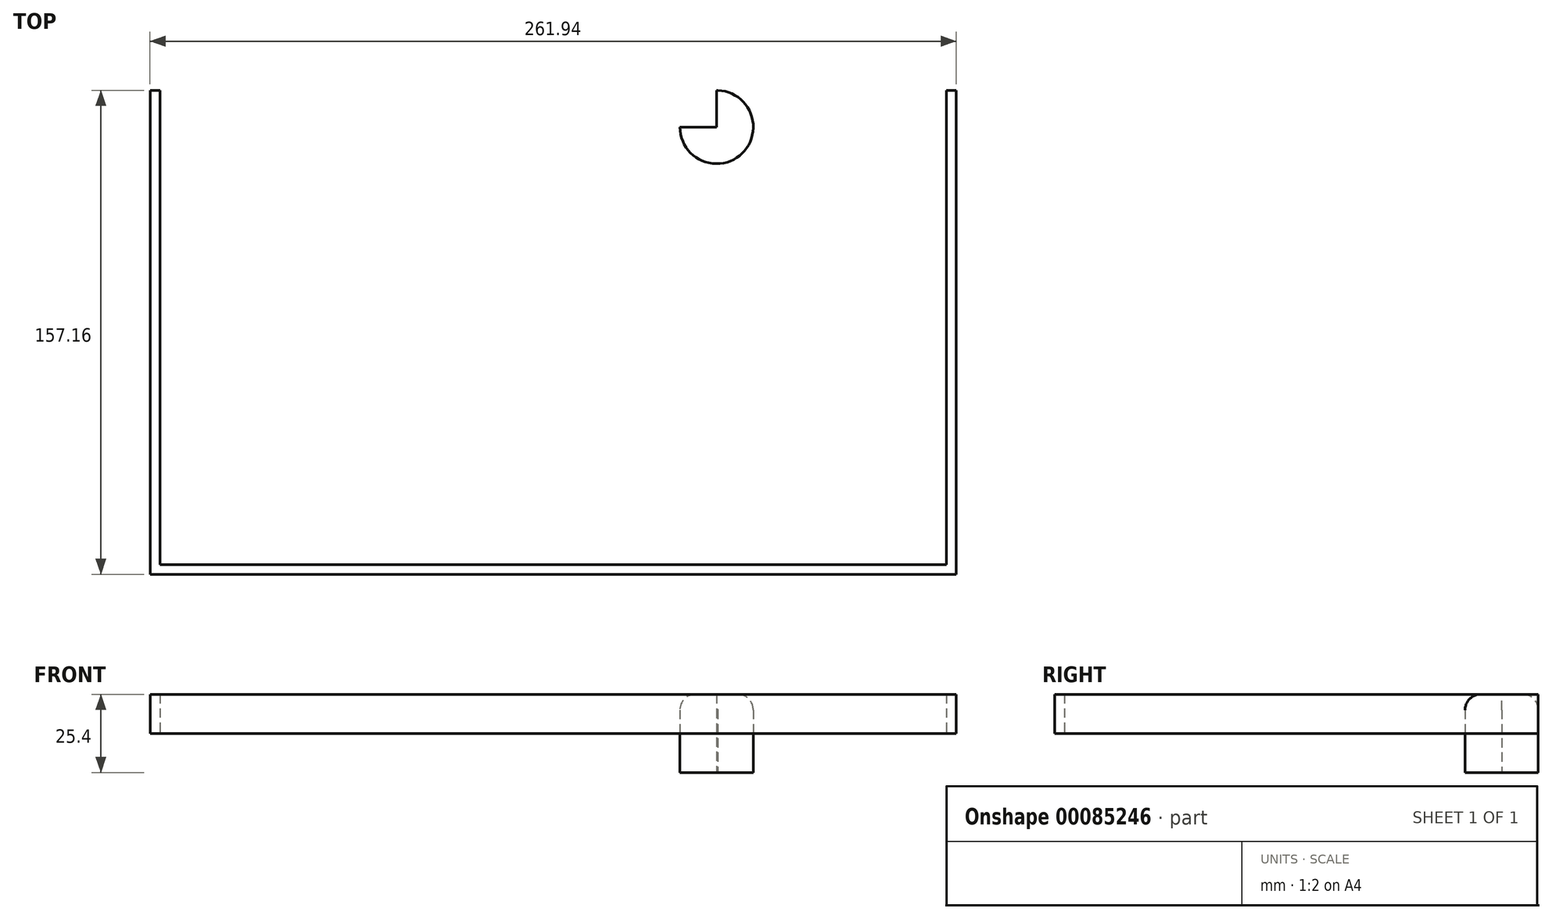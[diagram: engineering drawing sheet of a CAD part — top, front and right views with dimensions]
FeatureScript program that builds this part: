
annotation { "Feature Type Name" : "Feature", "Feature Type Description" : "" }
export const myFeature = defineFeature(function(context is Context, id is Id, definition is map)
    precondition{}
    {
        {
            var Q0;
            Q0=qCreatedBy(makeId("Top.planeOp"),FACE);
            var sketch = newSketch(context, id + "F0", { "sketchPlane" : qUnion([Q0])});
            skLineSegment(sketch, "E0.bottom", {"start": v(-130.97, 78.58) * mm, "end": v(130.97, 78.58) * mm});
            skLineSegment(sketch, "E0.top", {"start": v(-130.97, -78.58) * mm, "end": v(130.97, -78.58) * mm});
            skLineSegment(sketch, "E0.left", {"start": v(-130.97, 78.58) * mm, "end": v(-130.97, -78.58) * mm});
            skLineSegment(sketch, "E0.right", {"start": v(130.97, 78.58) * mm, "end": v(130.97, -78.58) * mm});
            skPoint(sketch, "E0.middle", {"position": v(0, 0) * mm});
            skSolve(sketch);
        }
        {
            var Q0;
            Q0=makeQuery(id+"F0.imprint","IMPRINT",FACE,{"disambiguationData":[TD([[makeQuery(id+"F0.imprint","IMPRINT",EDGE,{"derivedFrom":sQuery(id+"F0.wireOp",EDGE,"E0.bottom")}),-1.0]])]});
            extrude(context, id + "F1", {"entities" : qUnion([Q0]), "depth" : 12.7 * mm});
        }
        {
            var Q0;
            Q0=makeQuery(id+"F1.opExtrude","CAP_FACE",FACE,{"disambiguationData":[OSD([sQuery(id+"F0.wireOp",EDGE,"E0.bottom"),sQuery(id+"F0.wireOp",EDGE,"E0.top"),sQuery(id+"F0.wireOp",EDGE,"E0.left"),sQuery(id+"F0.wireOp",EDGE,"E0.right")])],"isStart":true});
            var sketch = newSketch(context, id + "F2", { "sketchPlane" : qUnion([Q0])});
            skLineSegment(sketch, "E1.bottom", {"start": v(127.8, -78.58) * mm, "end": v(-127.8, -78.58) * mm});
            skLineSegment(sketch, "E1.top", {"start": v(127.8, 75.4) * mm, "end": v(-127.8, 75.4) * mm});
            skLineSegment(sketch, "E1.left", {"start": v(127.8, -78.58) * mm, "end": v(127.8, 75.4) * mm});
            skLineSegment(sketch, "E1.right", {"start": v(-127.8, -78.58) * mm, "end": v(-127.8, 75.4) * mm});
            skSolve(sketch);
        }
        {
            var Q0;
            Q0=makeQuery(id+"F2.imprint","IMPRINT",FACE,{"disambiguationData":[TD([[makeQuery(id+"F2.imprint","IMPRINT",EDGE,{"derivedFrom":sQuery(id+"F2.wireOp",EDGE,"E1.bottom")}),1.0]])]});
            extrude(context, id + "F3", {"entities" : qUnion([Q0]), "operationType" : NewBodyOperationType.ADD, "depth" : 12.7 * mm});
        }
        {
            var Q0;
            Q0=makeQuery(id+"F3.opExtrude","CAP_FACE",FACE,{"disambiguationData":[OSD([sQuery(id+"F2.wireOp",EDGE,"E1.bottom"),sQuery(id+"F2.wireOp",EDGE,"E1.top"),sQuery(id+"F2.wireOp",EDGE,"E1.left"),sQuery(id+"F2.wireOp",EDGE,"E1.right")])],"isStart":false});
            var sketch = newSketch(context, id + "F4", { "sketchPlane" : qUnion([Q0])});
            skPoint(sketch, "E2", {"position": v(0, -68.27) * mm});
            skCircle(sketch, "E3", {"center": v(-10.32, -68.27) * mm, "radius": 10.32 * mm});
            skCircle(sketch, "E4", {"center": v(-30.95, -68.27) * mm, "radius": 10.33 * mm});
            skCircle(sketch, "E5", {"center": v(-53.13, -66.68) * mm, "radius": 11.9 * mm});
            skCircle(sketch, "E6.MirrorC", {"center": v(30.95, -68.27) * mm, "radius": 10.33 * mm});
            skCircle(sketch, "E7.MirrorC", {"center": v(10.32, -68.27) * mm, "radius": 10.32 * mm});
            skCircle(sketch, "E8.MirrorC", {"center": v(53.13, -66.68) * mm, "radius": 11.9 * mm});
            skPoint(sketch, "E9.middle", {"position": v(0, -78.58) * mm});
            skSolve(sketch);
        }
        {
            var Q0;
            {var subQ0=sQuery(id+"F4.wireOp",EDGE,"E4");var subQ1=sQuery(id+"F4.wireOp",EDGE,"E3");var subQ2=makeQuery(id+"F4.imprint","INTERSECT",VERTEX,{"disambiguationData":[OD(0.0)],"derivedFrom":[subQ1,subQ0]});Q0=makeQuery(id+"F4.imprint","IMPRINT",FACE,{"disambiguationData":[TD([[makeQuery(id+"F4.imprint","IMPRINT",EDGE,{"disambiguationData":[TD([[subQ2,1.0]])],"derivedFrom":subQ1}),1.0]])]});}
            var Q1;
            {var subQ0=sQuery(id+"F4.wireOp",EDGE,"E7.MirrorC");var subQ1=sQuery(id+"F4.wireOp",EDGE,"E6.MirrorC");var subQ2=makeQuery(id+"F4.imprint","INTERSECT",VERTEX,{"disambiguationData":[OD(0.0)],"derivedFrom":[subQ1,subQ0]});Q1=makeQuery(id+"F4.imprint","IMPRINT",FACE,{"disambiguationData":[TD([[makeQuery(id+"F4.imprint","IMPRINT",EDGE,{"disambiguationData":[TD([[subQ2,1.0]])],"derivedFrom":subQ1}),-1.0]])]});}
            var Q2;
            {var subQ0=sQuery(id+"F4.wireOp",EDGE,"E3");var subQ1=makeQuery(id+"F3.opExtrude","CAP_EDGE",EDGE,{"disambiguationData":[OSD([sQuery(id+"F2.wireOp",EDGE,"E1.bottom")])],"isStart":false});var subQ2=makeQuery(id+"F4.imprint","INTERSECT",VERTEX,{"disambiguationData":[OD(0.0)],"derivedFrom":[subQ1,subQ0]});Q2=makeQuery(id+"F4.imprint","IMPRINT",FACE,{"disambiguationData":[TD([[makeQuery(id+"F4.imprint","IMPRINT",EDGE,{"disambiguationData":[TD([[subQ2,-1.0]])],"derivedFrom":subQ0}),1.0]])]});}
            var Q3;
            {var subQ0=sQuery(id+"F4.wireOp",EDGE,"E4");var subQ1=makeQuery(id+"F3.opExtrude","CAP_EDGE",EDGE,{"disambiguationData":[OSD([sQuery(id+"F2.wireOp",EDGE,"E1.bottom")])],"isStart":false});var subQ2=makeQuery(id+"F4.imprint","INTERSECT",VERTEX,{"disambiguationData":[OD(0.0)],"derivedFrom":[subQ1,subQ0]});Q3=makeQuery(id+"F4.imprint","IMPRINT",FACE,{"disambiguationData":[TD([[makeQuery(id+"F4.imprint","IMPRINT",EDGE,{"disambiguationData":[TD([[subQ2,-1.0]])],"derivedFrom":subQ0}),1.0]])]});}
            var Q4;
            {var subQ0=sQuery(id+"F4.wireOp",EDGE,"E5");var subQ1=makeQuery(id+"F3.opExtrude","CAP_EDGE",EDGE,{"disambiguationData":[OSD([sQuery(id+"F2.wireOp",EDGE,"E1.bottom")])],"isStart":false});var subQ2=makeQuery(id+"F4.imprint","INTERSECT",VERTEX,{"disambiguationData":[OD(0.0)],"derivedFrom":[subQ1,subQ0]});Q4=makeQuery(id+"F4.imprint","IMPRINT",FACE,{"disambiguationData":[TD([[makeQuery(id+"F4.imprint","IMPRINT",EDGE,{"disambiguationData":[TD([[subQ2,-1.0]])],"derivedFrom":subQ0}),1.0]])]});}
            var Q5;
            {var subQ0=sQuery(id+"F4.wireOp",EDGE,"E6.MirrorC");var subQ1=makeQuery(id+"F3.opExtrude","CAP_EDGE",EDGE,{"disambiguationData":[OSD([sQuery(id+"F2.wireOp",EDGE,"E1.bottom")])],"isStart":false});var subQ2=makeQuery(id+"F4.imprint","INTERSECT",VERTEX,{"disambiguationData":[OD(0.0)],"derivedFrom":[subQ1,subQ0]});Q5=makeQuery(id+"F4.imprint","IMPRINT",FACE,{"disambiguationData":[TD([[makeQuery(id+"F4.imprint","IMPRINT",EDGE,{"disambiguationData":[TD([[subQ2,-1.0]])],"derivedFrom":subQ0}),-1.0]])]});}
            var Q6;
            {var subQ0=sQuery(id+"F4.wireOp",EDGE,"E7.MirrorC");var subQ1=makeQuery(id+"F3.opExtrude","CAP_EDGE",EDGE,{"disambiguationData":[OSD([sQuery(id+"F2.wireOp",EDGE,"E1.bottom")])],"isStart":false});var subQ2=makeQuery(id+"F4.imprint","INTERSECT",VERTEX,{"disambiguationData":[OD(0.0)],"derivedFrom":[subQ1,subQ0]});Q6=makeQuery(id+"F4.imprint","IMPRINT",FACE,{"disambiguationData":[TD([[makeQuery(id+"F4.imprint","IMPRINT",EDGE,{"disambiguationData":[TD([[subQ2,-1.0]])],"derivedFrom":subQ0}),-1.0]])]});}
            var Q7;
            {var subQ0=sQuery(id+"F4.wireOp",EDGE,"E8.MirrorC");var subQ1=makeQuery(id+"F3.opExtrude","CAP_EDGE",EDGE,{"disambiguationData":[OSD([sQuery(id+"F2.wireOp",EDGE,"E1.bottom")])],"isStart":false});var subQ2=makeQuery(id+"F4.imprint","INTERSECT",VERTEX,{"disambiguationData":[OD(0.0)],"derivedFrom":[subQ1,subQ0]});Q7=makeQuery(id+"F4.imprint","IMPRINT",FACE,{"disambiguationData":[TD([[makeQuery(id+"F4.imprint","IMPRINT",EDGE,{"disambiguationData":[TD([[subQ2,-1.0]])],"derivedFrom":subQ0}),-1.0]])]});}
            var Q8;
            {var subQ0=sQuery(id+"F4.wireOp",EDGE,"E8.MirrorC");var subQ1=makeQuery(id+"F3.opExtrude","CAP_EDGE",EDGE,{"disambiguationData":[OSD([sQuery(id+"F2.wireOp",EDGE,"E1.bottom")])],"isStart":false});var subQ2=makeQuery(id+"F4.imprint","INTERSECT",VERTEX,{"disambiguationData":[OD(0.0)],"derivedFrom":[subQ1,subQ0]});Q8=makeQuery(id+"F4.imprint","IMPRINT",FACE,{"disambiguationData":[TD([[makeQuery(id+"F4.imprint","IMPRINT",EDGE,{"disambiguationData":[TD([[subQ2,1.0]])],"derivedFrom":subQ0}),-1.0]])]});}
            var Q9;
            {var subQ0=sQuery(id+"F4.wireOp",EDGE,"E4");var subQ1=sQuery(id+"F4.wireOp",EDGE,"E3");var subQ2=makeQuery(id+"F4.imprint","INTERSECT",VERTEX,{"disambiguationData":[OD(0.0)],"derivedFrom":[subQ1,subQ0]});Q9=makeQuery(id+"F4.imprint","IMPRINT",FACE,{"disambiguationData":[TD([[makeQuery(id+"F4.imprint","IMPRINT",EDGE,{"disambiguationData":[TD([[subQ2,-1.0]])],"derivedFrom":subQ1}),1.0]])]});}
            var Q10;
            {var subQ0=sQuery(id+"F4.wireOp",EDGE,"E7.MirrorC");var subQ1=sQuery(id+"F4.wireOp",EDGE,"E6.MirrorC");var subQ2=makeQuery(id+"F4.imprint","INTERSECT",VERTEX,{"disambiguationData":[OD(0.0)],"derivedFrom":[subQ1,subQ0]});Q10=makeQuery(id+"F4.imprint","IMPRINT",FACE,{"disambiguationData":[TD([[makeQuery(id+"F4.imprint","IMPRINT",EDGE,{"disambiguationData":[TD([[subQ2,-1.0]])],"derivedFrom":subQ1}),-1.0]])]});}
            var Q11;
            {var subQ0=sQuery(id+"F4.wireOp",EDGE,"E7.MirrorC");var subQ1=sQuery(id+"F4.wireOp",EDGE,"E6.MirrorC");var subQ2=makeQuery(id+"F4.imprint","INTERSECT",VERTEX,{"disambiguationData":[OD(0.0)],"derivedFrom":[subQ1,subQ0]});Q11=makeQuery(id+"F4.imprint","IMPRINT",FACE,{"disambiguationData":[TD([[makeQuery(id+"F4.imprint","IMPRINT",EDGE,{"disambiguationData":[TD([[subQ2,1.0]])],"derivedFrom":subQ1}),1.0]])]});}
            var Q12;
            {var subQ0=sQuery(id+"F4.wireOp",EDGE,"E4");var subQ1=sQuery(id+"F4.wireOp",EDGE,"E3");var subQ2=makeQuery(id+"F4.imprint","INTERSECT",VERTEX,{"disambiguationData":[OD(0.0)],"derivedFrom":[subQ1,subQ0]});Q12=makeQuery(id+"F4.imprint","IMPRINT",FACE,{"disambiguationData":[TD([[makeQuery(id+"F4.imprint","IMPRINT",EDGE,{"disambiguationData":[TD([[subQ2,1.0]])],"derivedFrom":subQ1}),-1.0]])]});}
            var Q13;
            {var subQ0=sQuery(id+"F4.wireOp",EDGE,"E5");var subQ1=makeQuery(id+"F3.opExtrude","CAP_EDGE",EDGE,{"disambiguationData":[OSD([sQuery(id+"F2.wireOp",EDGE,"E1.bottom")])],"isStart":false});var subQ2=makeQuery(id+"F4.imprint","INTERSECT",VERTEX,{"disambiguationData":[OD(0.0)],"derivedFrom":[subQ1,subQ0]});Q13=makeQuery(id+"F4.imprint","IMPRINT",FACE,{"disambiguationData":[TD([[makeQuery(id+"F4.imprint","IMPRINT",EDGE,{"disambiguationData":[TD([[subQ2,1.0]])],"derivedFrom":subQ0}),1.0]])]});}
            var Q14;
            {var subQ0=sQuery(id+"F4.wireOp",EDGE,"E4");var subQ1=sQuery(id+"F4.wireOp",EDGE,"E3");var subQ2=makeQuery(id+"F4.imprint","INTERSECT",VERTEX,{"disambiguationData":[OD(0.0)],"derivedFrom":[subQ1,subQ0]});Q14=makeQuery(id+"F4.imprint","IMPRINT",FACE,{"disambiguationData":[TD([[makeQuery(id+"F4.imprint","IMPRINT",EDGE,{"disambiguationData":[TD([[subQ2,-1.0]])],"derivedFrom":subQ1}),-1.0]])]});}
            var Q15;
            {var subQ0=sQuery(id+"F4.wireOp",EDGE,"E7.MirrorC");var subQ1=sQuery(id+"F4.wireOp",EDGE,"E6.MirrorC");var subQ2=makeQuery(id+"F4.imprint","INTERSECT",VERTEX,{"disambiguationData":[OD(1.0)],"derivedFrom":[subQ1,subQ0]});Q15=makeQuery(id+"F4.imprint","IMPRINT",FACE,{"disambiguationData":[TD([[makeQuery(id+"F4.imprint","IMPRINT",EDGE,{"disambiguationData":[TD([[subQ2,1.0]])],"derivedFrom":subQ1}),1.0]])]});}
            extrude(context, id + "F5", {"entities" : qUnion([Q0, Q1, Q2, Q3, Q4, Q5, Q6, Q7, Q8, Q9, Q10, Q11, Q12, Q13, Q14, Q15]), "operationType" : NewBodyOperationType.REMOVE, "endBound" : BoundingType.THROUGH_ALL, "oppositeDirection" : true, "depth" : 25.4 * mm});
        }
        {
            var Q0;
            Q0=makeQuery(id+"F3.opExtrude","CAP_FACE",FACE,{"disambiguationData":[OSD([sQuery(id+"F2.wireOp",EDGE,"E1.bottom"),sQuery(id+"F2.wireOp",EDGE,"E1.top"),sQuery(id+"F2.wireOp",EDGE,"E1.left"),sQuery(id+"F2.wireOp",EDGE,"E1.right")])],"isStart":false});
            var sketch = newSketch(context, id + "F6", { "sketchPlane" : qUnion([Q0])});
            skLineSegment(sketch, "E10.bottom", {"start": v(-53.13, -66.68) * mm, "end": v(53.13, -66.68) * mm});
            skLineSegment(sketch, "E10.top", {"start": v(-53.13, -90.48) * mm, "end": v(53.13, -90.48) * mm});
            skLineSegment(sketch, "E10.left", {"start": v(-53.13, -66.68) * mm, "end": v(-53.13, -90.48) * mm});
            skLineSegment(sketch, "E10.right", {"start": v(53.13, -66.68) * mm, "end": v(53.13, -90.48) * mm});
            skPoint(sketch, "E10.middle", {"position": v(0, -78.58) * mm});
            skSolve(sketch);
        }
        {
            var Q0;
            {var subQ0=sQuery(id+"F6.wireOp",EDGE,"E10.bottom");var subQ1=sQuery(id+"F4.wireOp",EDGE,"E5");var subQ2=makeQuery(id+"F5.boolean.opBoolean","COPY",EDGE,{"derivedFrom":makeQuery(id+"F5.opExtrude","CAP_EDGE",EDGE,{"disambiguationData":[OSD([subQ1])],"isStart":true})});var subQ3=makeQuery(id+"F6.imprint","INTERSECT",VERTEX,{"derivedFrom":[subQ2,subQ0]});Q0=makeQuery(id+"F6.imprint","IMPRINT",FACE,{"disambiguationData":[TD([[makeQuery(id+"F6.imprint","IMPRINT",EDGE,{"disambiguationData":[TD([[subQ3,-1.0]])],"derivedFrom":subQ0}),-1.0]])]});}
            var Q1;
            {var subQ0=sQuery(id+"F6.wireOp",EDGE,"E10.bottom");var subQ1=sQuery(id+"F4.wireOp",EDGE,"E3");var subQ2=makeQuery(id+"F5.boolean.opBoolean","COPY",EDGE,{"derivedFrom":makeQuery(id+"F5.opExtrude","CAP_EDGE",EDGE,{"disambiguationData":[OSD([subQ1])],"isStart":true})});var subQ3=makeQuery(id+"F6.imprint","INTERSECT",VERTEX,{"disambiguationData":[OD(1.0)],"derivedFrom":[subQ2,subQ0]});Q1=makeQuery(id+"F6.imprint","IMPRINT",FACE,{"disambiguationData":[TD([[makeQuery(id+"F6.imprint","IMPRINT",EDGE,{"disambiguationData":[TD([[subQ3,-1.0]])],"derivedFrom":subQ0}),-1.0]])]});}
            var Q2;
            {var subQ0=sQuery(id+"F6.wireOp",EDGE,"E10.bottom");var subQ1=sQuery(id+"F4.wireOp",EDGE,"E8.MirrorC");var subQ2=makeQuery(id+"F5.boolean.opBoolean","COPY",EDGE,{"derivedFrom":makeQuery(id+"F5.opExtrude","CAP_EDGE",EDGE,{"disambiguationData":[OSD([subQ1])],"isStart":true})});var subQ3=makeQuery(id+"F6.imprint","INTERSECT",VERTEX,{"derivedFrom":[subQ2,subQ0]});Q2=makeQuery(id+"F6.imprint","IMPRINT",FACE,{"disambiguationData":[TD([[makeQuery(id+"F6.imprint","IMPRINT",EDGE,{"disambiguationData":[TD([[subQ3,1.0]])],"derivedFrom":subQ0}),-1.0]])]});}
            extrude(context, id + "F7", {"entities" : qUnion([Q0, Q1, Q2]), "operationType" : NewBodyOperationType.REMOVE, "endBound" : BoundingType.THROUGH_ALL, "oppositeDirection" : true, "depth" : 25.4 * mm});
        }
        {
            var Q0;
            Q0=makeQuery(id+"F5.boolean.opBoolean","INTERSECT",EDGE,{"disambiguationData":[OD(0.0)],"derivedFrom":[makeQuery(id+"F3.boolean.opBoolean","MERGE",FACE,{"derivedFrom":[makeQuery(id+"F1.opExtrude","SWEPT_FACE",FACE,{"disambiguationData":[OSD([sQuery(id+"F0.wireOp",EDGE,"E0.bottom")])]}),makeQuery(id+"F3.opExtrude","SWEPT_FACE",FACE,{"disambiguationData":[OSD([sQuery(id+"F2.wireOp",EDGE,"E1.bottom")])]})]}),makeQuery(id+"F5.opExtrude","SWEPT_FACE",FACE,{"disambiguationData":[OSD([sQuery(id+"F4.wireOp",EDGE,"E5")])]})]});
            var Q1;
            Q1=makeQuery(id+"F5.boolean.opBoolean","INTERSECT",EDGE,{"disambiguationData":[OD(0.0)],"derivedFrom":[makeQuery(id+"F3.boolean.opBoolean","MERGE",FACE,{"derivedFrom":[makeQuery(id+"F1.opExtrude","SWEPT_FACE",FACE,{"disambiguationData":[OSD([sQuery(id+"F0.wireOp",EDGE,"E0.bottom")])]}),makeQuery(id+"F3.opExtrude","SWEPT_FACE",FACE,{"disambiguationData":[OSD([sQuery(id+"F2.wireOp",EDGE,"E1.bottom")])]})]}),makeQuery(id+"F5.opExtrude","SWEPT_FACE",FACE,{"disambiguationData":[OSD([sQuery(id+"F4.wireOp",EDGE,"E8.MirrorC")])]})]});
            var Q2;
            Q2=makeQuery(id+"F1.opExtrude","CAP_EDGE",EDGE,{"disambiguationData":[OSD([sQuery(id+"F0.wireOp",EDGE,"E0.top")])],"isStart":false});
            var Q3;
            Q3=makeQuery(id+"F1.opExtrude","CAP_EDGE",EDGE,{"disambiguationData":[OSD([sQuery(id+"F0.wireOp",EDGE,"E0.right")])],"isStart":false});
            var Q4;
            Q4=makeQuery(id+"F1.opExtrude","SWEPT_EDGE",EDGE,{"disambiguationData":[OSD([sQuery(id+"F0.wireOp",EDGE,"E0.top"),sQuery(id+"F0.wireOp",EDGE,"E0.right")])]});
            var Q5;
            Q5=makeQuery(id+"F1.opExtrude","CAP_EDGE",EDGE,{"disambiguationData":[OSD([sQuery(id+"F0.wireOp",EDGE,"E0.left")])],"isStart":false});
            var Q6;
            Q6=makeQuery(id+"F1.opExtrude","SWEPT_EDGE",EDGE,{"disambiguationData":[OSD([sQuery(id+"F0.wireOp",EDGE,"E0.top"),sQuery(id+"F0.wireOp",EDGE,"E0.left")])]});
            var Q7;
            Q7=makeQuery(id+"F5.boolean.opBoolean","COPY",EDGE,{"derivedFrom":makeQuery(id+"F5.opExtrude","CAP_EDGE",EDGE,{"disambiguationData":[OSD([sQuery(id+"F4.wireOp",EDGE,"E8.MirrorC")])],"isStart":true})});
            var Q8;
            Q8=makeQuery(id+"F5.boolean.opBoolean","COPY",EDGE,{"derivedFrom":makeQuery(id+"F5.opExtrude","CAP_EDGE",EDGE,{"disambiguationData":[OSD([sQuery(id+"F4.wireOp",EDGE,"E6.MirrorC")])],"isStart":true})});
            var Q9;
            Q9=makeQuery(id+"F5.boolean.opBoolean","COPY",EDGE,{"derivedFrom":makeQuery(id+"F5.opExtrude","CAP_EDGE",EDGE,{"disambiguationData":[OSD([sQuery(id+"F4.wireOp",EDGE,"E7.MirrorC")])],"isStart":true})});
            var Q10;
            Q10=makeQuery(id+"F5.boolean.opBoolean","COPY",EDGE,{"derivedFrom":makeQuery(id+"F5.opExtrude","CAP_EDGE",EDGE,{"disambiguationData":[OSD([sQuery(id+"F4.wireOp",EDGE,"E3")])],"isStart":true})});
            var Q11;
            Q11=makeQuery(id+"F5.boolean.opBoolean","COPY",EDGE,{"derivedFrom":makeQuery(id+"F5.opExtrude","CAP_EDGE",EDGE,{"disambiguationData":[OSD([sQuery(id+"F4.wireOp",EDGE,"E4")])],"isStart":true})});
            var Q12;
            Q12=makeQuery(id+"F5.boolean.opBoolean","COPY",EDGE,{"derivedFrom":makeQuery(id+"F5.opExtrude","CAP_EDGE",EDGE,{"disambiguationData":[OSD([sQuery(id+"F4.wireOp",EDGE,"E5")])],"isStart":true})});
            var Q13;
            Q13=makeQuery(id+"F5.boolean.opBoolean","INTERSECT",EDGE,{"derivedFrom":[makeQuery(id+"F1.opExtrude","CAP_FACE",FACE,{"disambiguationData":[OSD([sQuery(id+"F0.wireOp",EDGE,"E0.bottom"),sQuery(id+"F0.wireOp",EDGE,"E0.top"),sQuery(id+"F0.wireOp",EDGE,"E0.left"),sQuery(id+"F0.wireOp",EDGE,"E0.right")])],"isStart":false}),makeQuery(id+"F5.opExtrude","SWEPT_FACE",FACE,{"disambiguationData":[OSD([sQuery(id+"F4.wireOp",EDGE,"E8.MirrorC")])]})]});
            var Q14;
            Q14=makeQuery(id+"F5.boolean.opBoolean","INTERSECT",EDGE,{"derivedFrom":[makeQuery(id+"F1.opExtrude","CAP_FACE",FACE,{"disambiguationData":[OSD([sQuery(id+"F0.wireOp",EDGE,"E0.bottom"),sQuery(id+"F0.wireOp",EDGE,"E0.top"),sQuery(id+"F0.wireOp",EDGE,"E0.left"),sQuery(id+"F0.wireOp",EDGE,"E0.right")])],"isStart":false}),makeQuery(id+"F5.opExtrude","SWEPT_FACE",FACE,{"disambiguationData":[OSD([sQuery(id+"F4.wireOp",EDGE,"E6.MirrorC")])]})]});
            var Q15;
            Q15=makeQuery(id+"F5.boolean.opBoolean","INTERSECT",EDGE,{"derivedFrom":[makeQuery(id+"F1.opExtrude","CAP_FACE",FACE,{"disambiguationData":[OSD([sQuery(id+"F0.wireOp",EDGE,"E0.bottom"),sQuery(id+"F0.wireOp",EDGE,"E0.top"),sQuery(id+"F0.wireOp",EDGE,"E0.left"),sQuery(id+"F0.wireOp",EDGE,"E0.right")])],"isStart":false}),makeQuery(id+"F5.opExtrude","SWEPT_FACE",FACE,{"disambiguationData":[OSD([sQuery(id+"F4.wireOp",EDGE,"E7.MirrorC")])]})]});
            var Q16;
            Q16=makeQuery(id+"F5.boolean.opBoolean","INTERSECT",EDGE,{"derivedFrom":[makeQuery(id+"F1.opExtrude","CAP_FACE",FACE,{"disambiguationData":[OSD([sQuery(id+"F0.wireOp",EDGE,"E0.bottom"),sQuery(id+"F0.wireOp",EDGE,"E0.top"),sQuery(id+"F0.wireOp",EDGE,"E0.left"),sQuery(id+"F0.wireOp",EDGE,"E0.right")])],"isStart":false}),makeQuery(id+"F5.opExtrude","SWEPT_FACE",FACE,{"disambiguationData":[OSD([sQuery(id+"F4.wireOp",EDGE,"E3")])]})]});
            var Q17;
            Q17=makeQuery(id+"F5.boolean.opBoolean","INTERSECT",EDGE,{"derivedFrom":[makeQuery(id+"F1.opExtrude","CAP_FACE",FACE,{"disambiguationData":[OSD([sQuery(id+"F0.wireOp",EDGE,"E0.bottom"),sQuery(id+"F0.wireOp",EDGE,"E0.top"),sQuery(id+"F0.wireOp",EDGE,"E0.left"),sQuery(id+"F0.wireOp",EDGE,"E0.right")])],"isStart":false}),makeQuery(id+"F5.opExtrude","SWEPT_FACE",FACE,{"disambiguationData":[OSD([sQuery(id+"F4.wireOp",EDGE,"E4")])]})]});
            var Q18;
            Q18=makeQuery(id+"F5.boolean.opBoolean","INTERSECT",EDGE,{"derivedFrom":[makeQuery(id+"F1.opExtrude","CAP_FACE",FACE,{"disambiguationData":[OSD([sQuery(id+"F0.wireOp",EDGE,"E0.bottom"),sQuery(id+"F0.wireOp",EDGE,"E0.top"),sQuery(id+"F0.wireOp",EDGE,"E0.left"),sQuery(id+"F0.wireOp",EDGE,"E0.right")])],"isStart":false}),makeQuery(id+"F5.opExtrude","SWEPT_FACE",FACE,{"disambiguationData":[OSD([sQuery(id+"F4.wireOp",EDGE,"E5")])]})]});
            fillet(context, id + "F8", {"entities" : qUnion([Q0, Q1, Q2, Q3, Q4, Q5, Q6, Q7, Q8, Q9, Q10, Q11, Q12, Q13, Q14, Q15, Q16, Q17, Q18]), "radius" : 5.08 * mm, "tangentPropagation" : true, "allowEdgeOverflow" : false});
        }
    });
